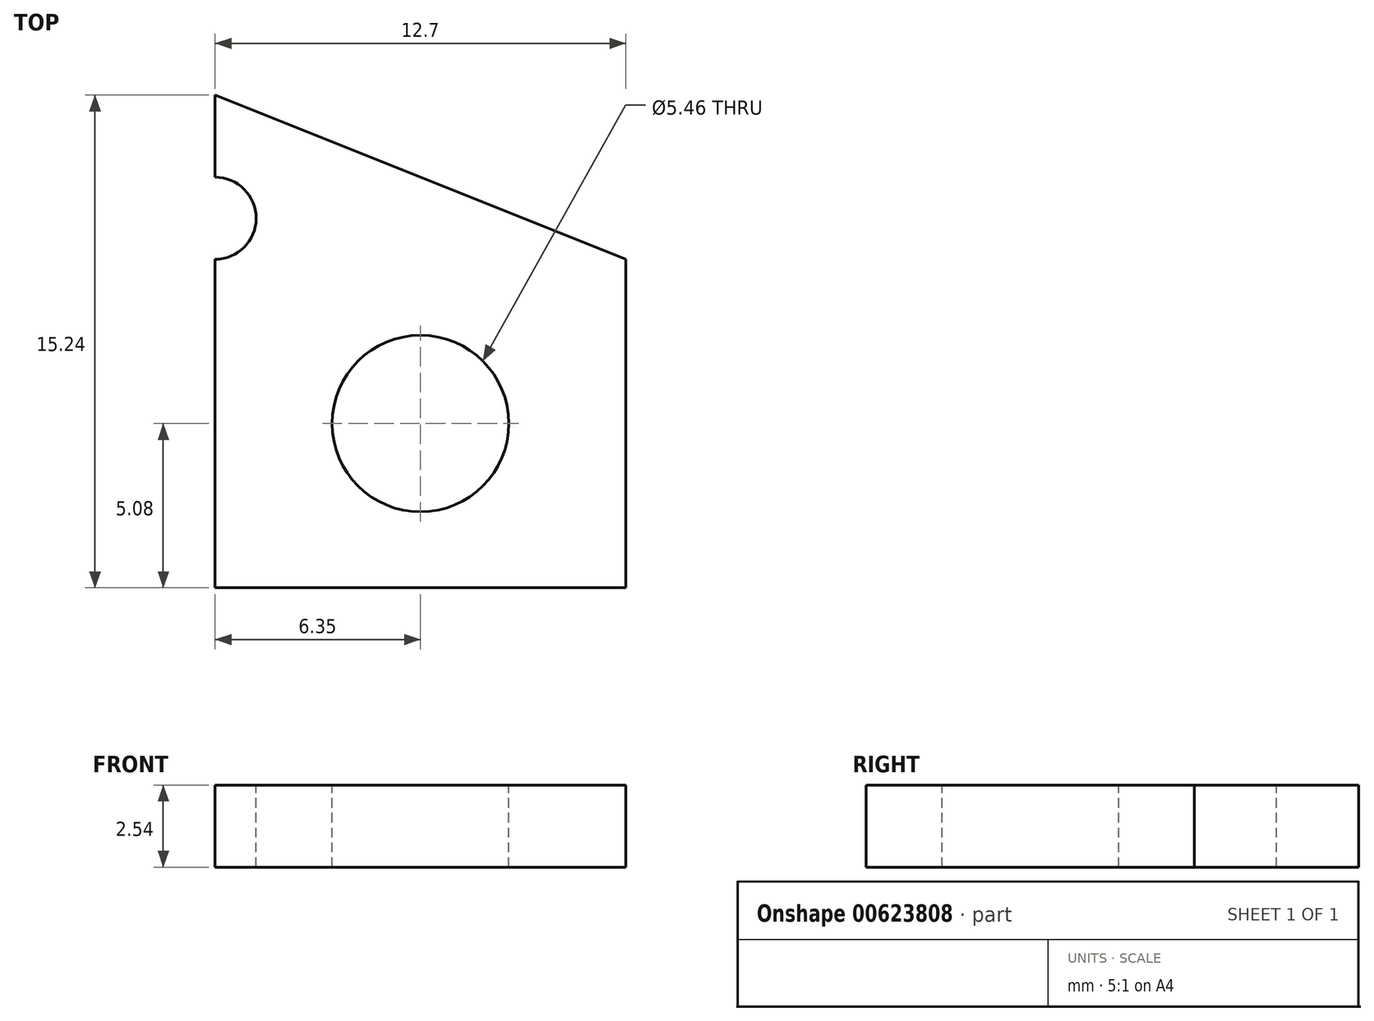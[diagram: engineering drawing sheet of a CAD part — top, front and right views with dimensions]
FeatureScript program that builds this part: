
annotation { "Feature Type Name" : "Feature", "Feature Type Description" : "" }
export const myFeature = defineFeature(function(context is Context, id is Id, definition is map)
    precondition{}
    {
        {
            var Q0;
            Q0=qCreatedBy(makeId("Top.planeOp"),FACE);
            var sketch = newSketch(context, id + "F0", { "sketchPlane" : qUnion([Q0])});
            skLineSegment(sketch, "E0.bottom", {"start": v(6.35, -5.08) * mm, "end": v(-6.35, -5.08) * mm});
            skLineSegment(sketch, "E0.top", {"start": v(6.35, 5.08) * mm, "end": v(-6.35, 5.08) * mm});
            skLineSegment(sketch, "E0.left", {"start": v(6.35, -5.08) * mm, "end": v(6.35, 5.08) * mm});
            skLineSegment(sketch, "E0.right", {"start": v(-6.35, -5.08) * mm, "end": v(-6.35, 5.08) * mm});
            skPoint(sketch, "E0.middle", {"position": v(0, 0) * mm});
            skLineSegment(sketch, "E1", {"start": v(-6.35, 5.08) * mm, "end": v(-6.35, 10.16) * mm});
            skLineSegment(sketch, "E2", {"start": v(-6.35, 10.16) * mm, "end": v(6.35, 5.08) * mm});
            skSolve(sketch);
        }
        {
            var Q0;
            Q0 = qSketchRegion(id + "F0", true);
            extrude(context, id + "F1", {"entities" : qUnion([Q0]), "depth" : 2.54 * mm, "offsetDistance" : 25.4 * mm});
        }
        {
            var Q0;
            Q0=makeQuery(id+"F1.opExtrude","CAP_FACE",FACE,{"disambiguationData":[OSD([sQuery(id+"F0.wireOp",EDGE,"E0.bottom"),sQuery(id+"F0.wireOp",EDGE,"E0.left"),sQuery(id+"F0.wireOp",EDGE,"E0.right"),sQuery(id+"F0.wireOp",EDGE,"E1"),sQuery(id+"F0.wireOp",EDGE,"E2")])],"isStart":false});
            var sketch = newSketch(context, id + "F2", { "sketchPlane" : qUnion([Q0])});
            skLineSegment(sketch, "E3", {"start": v(0, 0) * mm, "end": v(-6.35, 0) * mm});
            skLineSegment(sketch, "E4", {"start": v(-6.35, 0) * mm, "end": v(-6.35, 6.35) * mm});
            skCircle(sketch, "E5", {"center": v(-6.35, 6.35) * mm, "radius": 1.27 * mm});
            skSolve(sketch);
        }
        {
            var Q0;
            Q0 = qSketchRegion(id + "F2", true);
            extrude(context, id + "F3", {"entities" : qUnion([Q0]), "operationType" : NewBodyOperationType.REMOVE, "oppositeDirection" : true, "depth" : 25.4 * mm, "offsetDistance" : 25.4 * mm});
        }
        {
            var Q0;
            Q0=makeQuery(id+"F1.opExtrude","CAP_FACE",FACE,{"disambiguationData":[OSD([sQuery(id+"F0.wireOp",EDGE,"E0.bottom"),sQuery(id+"F0.wireOp",EDGE,"E0.left"),sQuery(id+"F0.wireOp",EDGE,"E0.right"),sQuery(id+"F0.wireOp",EDGE,"E1"),sQuery(id+"F0.wireOp",EDGE,"E2")])],"isStart":false});
            var sketch = newSketch(context, id + "F4", { "sketchPlane" : qUnion([Q0])});
            skCircle(sketch, "E6", {"center": v(0, 0) * mm, "radius": 2.73 * mm});
            skSolve(sketch);
        }
        {
            var Q0;
            Q0 = qSketchRegion(id + "F4", true);
            extrude(context, id + "F5", {"entities" : qUnion([Q0]), "operationType" : NewBodyOperationType.REMOVE, "oppositeDirection" : true, "depth" : 25.4 * mm, "offsetDistance" : 25.4 * mm});
        }
    });
